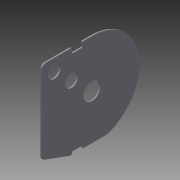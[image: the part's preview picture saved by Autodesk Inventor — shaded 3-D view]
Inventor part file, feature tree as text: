
AUTODESK INVENTOR PART (.ipt)
format: ipt  version: 2015 (Build 190159000, 159)  size: 142,336 bytes
history: native  units: mm
features: fillet x2, extrude x1, sketch x1
ambient origin geometry x8: Origin, YZ Plane, XZ Plane, XY Plane, X Axis, Y Axis, Z Axis, Center Point
bodies: Body1 (feature_tree)
feature tree (4):
  extrude  "Extrusion3"  Depth=1.5mm
  fillet  "Fillet1"  Radius=15.0mm
  fillet  "Fillet2"  Radius=15.0mm
  sketch  "Sketch1"  dims[d3=32.5mm d4=94.0mm d6=15.0mm d7=15.0mm d8=60.0mm d9=20.0mm d13=52.0mm d18=55.0mm d20=100.0mm d31=55.0mm d34=58.0mm d50=1.5mm d51=0.0mm d52=5.0mm d54=47.0mm d56=1.0mm d59=20.0mm d60=12.0mm d61=6.0mm d65=0.5mm d69=95.0mm d70=5.0mm d72=19.198622mm d73=3.0mm d74=12.0mm d75=1.5mm]
